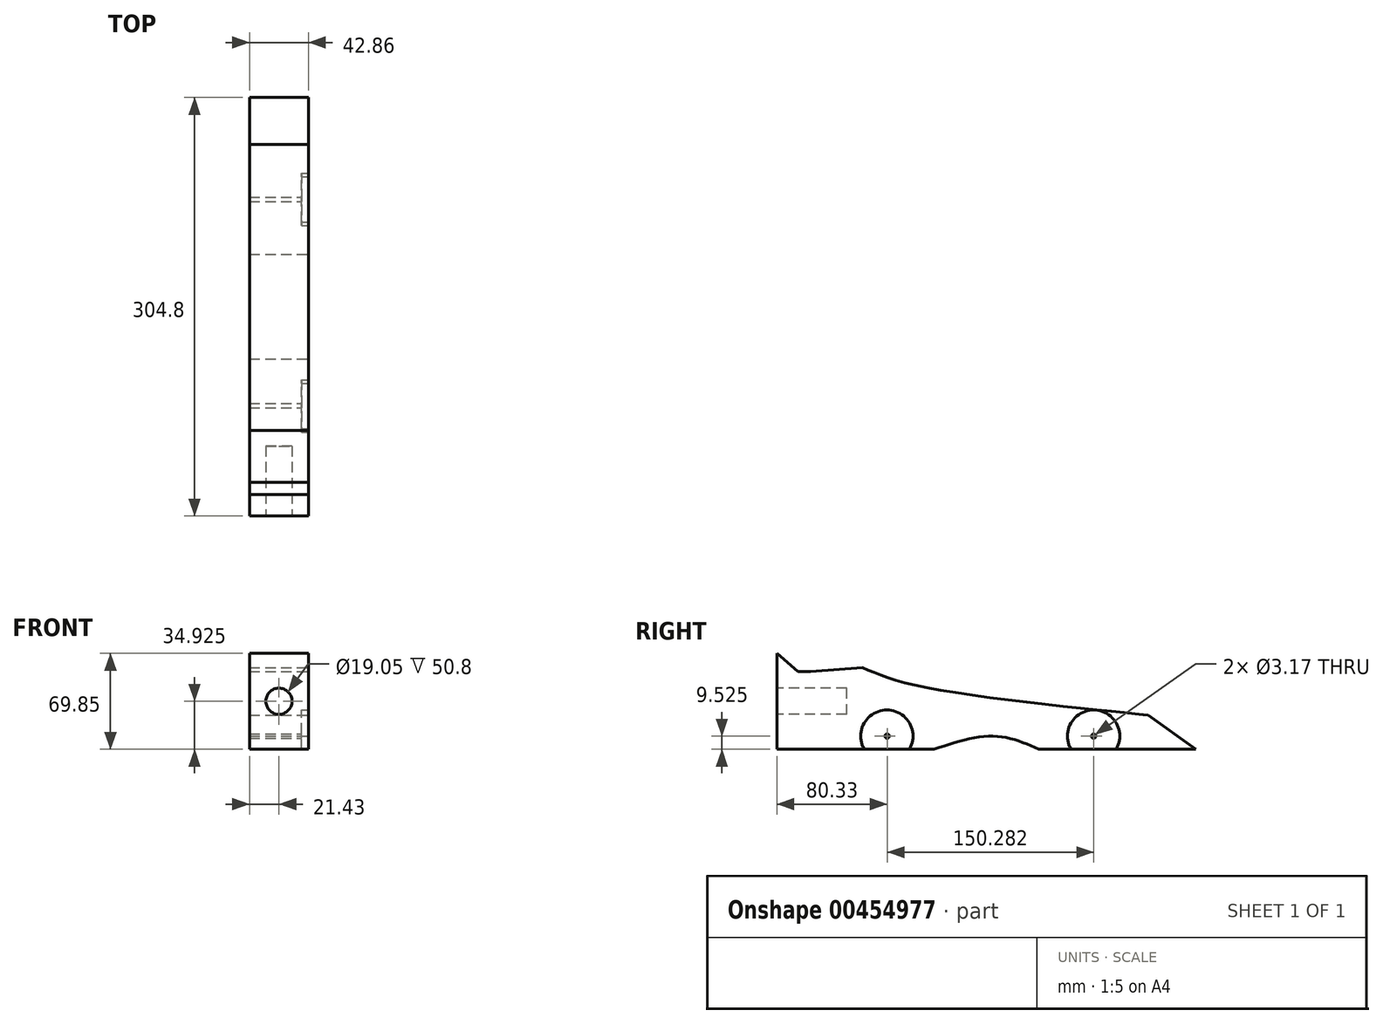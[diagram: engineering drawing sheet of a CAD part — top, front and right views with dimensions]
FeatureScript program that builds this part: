
annotation { "Feature Type Name" : "Feature", "Feature Type Description" : "" }
export const myFeature = defineFeature(function(context is Context, id is Id, definition is map)
    precondition{}
    {
        {
            var Q0;
            Q0=qCreatedBy(makeId("Right.planeOp"),FACE);
            var sketch = newSketch(context, id + "F0", { "sketchPlane" : qUnion([Q0])});
            skLineSegment(sketch, "E0", {"start": v(-152.4, 0) * mm, "end": v(152.4, 0) * mm});
            skLineSegment(sketch, "E1", {"start": v(-152.4, 0) * mm, "end": v(-152.4, 69.85) * mm});
            skLineSegment(sketch, "E2", {"start": v(152.4, 0) * mm, "end": v(152.4, 19.05) * mm});
            skLineSegment(sketch, "E3", {"start": v(152.4, 19.05) * mm, "end": v(-152.4, 69.85) * mm});
            skPoint(sketch, "E4.endSnap0", {"position": v(-152.4, 34.93) * mm});
            skLineSegment(sketch, "E5.0", {"start": v(-95.25, 50.8) * mm, "end": v(-152.4, 50.8) * mm, "construction": true});
            skLineSegment(sketch, "E5.1", {"start": v(-95.25, 50.8) * mm, "end": v(-95.25, 19.05) * mm, "construction": true});
            skLineSegment(sketch, "E5.2", {"start": v(-95.25, 19.05) * mm, "end": v(-152.4, 19.05) * mm, "construction": true});
            skSolve(sketch);
        }
        {
            var Q0;
            Q0=makeQuery(id+"F0.imprint","IMPRINT",FACE,{"disambiguationData":[TD([[makeQuery(id+"F0.imprint","IMPRINT",EDGE,{"derivedFrom":sQuery(id+"F0.wireOp",EDGE,"E0")}),1.0]])]});
            extrude(context, id + "F1", {"entities" : qUnion([Q0]), "depth" : 42.86 * mm, "symmetric" : true});
        }
        {
            var Q0;
            Q0=makeQuery(id+"F1.opExtrude","SWEPT_FACE",FACE,{"disambiguationData":[OSD([sQuery(id+"F0.wireOp",EDGE,"E1")])]});
            var sketch = newSketch(context, id + "F2", { "sketchPlane" : qUnion([Q0])});
            skLineSegment(sketch, "E6", {"start": v(21.43, 34.93) * mm, "end": v(0, 34.93) * mm, "construction": true});
            skCircle(sketch, "E7", {"center": v(0, 34.93) * mm, "radius": 9.53 * mm});
            skSolve(sketch);
        }
        {
            var Q0;
            Q0=makeQuery(id+"F2.imprint","IMPRINT",FACE,{"disambiguationData":[TD([[makeQuery(id+"F2.imprint","IMPRINT",EDGE,{"derivedFrom":sQuery(id+"F2.wireOp",EDGE,"E7")}),1.0]])]});
            var Q1;
            Q1=sQuery(id+"F2.wireOp",EDGE,"E7");
            extrude(context, id + "F3", {"entities" : qUnion([Q0]), "operationType" : NewBodyOperationType.REMOVE, "surfaceEntities" : qUnion([Q1]), "oppositeDirection" : true, "depth" : 50.8 * mm});
        }
        {
            var Q0;
            Q0=makeQuery(id+"F1.opExtrude","CAP_FACE",FACE,{"disambiguationData":[OSD([sQuery(id+"F0.wireOp",EDGE,"E0"),sQuery(id+"F0.wireOp",EDGE,"E1"),sQuery(id+"F0.wireOp",EDGE,"E2"),sQuery(id+"F0.wireOp",EDGE,"E3")])],"isStart":false});
            var sketch = newSketch(context, id + "F4", { "sketchPlane" : qUnion([Q0])});
            skLineSegment(sketch, "E8", {"start": v(-152.4, 34.93) * mm, "end": v(-152.4, 44.45) * mm, "construction": true});
            skLineSegment(sketch, "E9.0", {"start": v(-95.25, 19.05) * mm, "end": v(-152.4, 19.05) * mm, "construction": true});
            skLineSegment(sketch, "E9.1", {"start": v(-95.25, 50.8) * mm, "end": v(-95.25, 19.05) * mm, "construction": true});
            skLineSegment(sketch, "E9.2", {"start": v(-152.4, 50.8) * mm, "end": v(-95.25, 50.8) * mm, "construction": true});
            skLineSegment(sketch, "E10", {"start": v(57.15, 0) * mm, "end": v(57.15, 34.93) * mm, "construction": true});
            skLineSegment(sketch, "E11", {"start": v(-152.4, 44.45) * mm, "end": v(-101.6, 44.45) * mm, "construction": true});
            skLineSegment(sketch, "E12", {"start": v(-101.6, 44.45) * mm, "end": v(-101.6, 25.4) * mm, "construction": true});
            skLineSegment(sketch, "E13", {"start": v(-101.6, 25.4) * mm, "end": v(-152.4, 25.4) * mm, "construction": true});
            skLineSegment(sketch, "E14", {"start": v(118.06, 24.77) * mm, "end": v(152.4, 0) * mm});
            skLineSegment(sketch, "E15", {"start": v(-136.93, 67.27) * mm, "end": v(-136.93, 56.65) * mm});
            skLineSegment(sketch, "E16", {"start": v(-136.93, 56.65) * mm, "end": v(-127.78, 56.65) * mm});
            skLineSegment(sketch, "E17", {"start": v(-127.78, 56.65) * mm, "end": v(-127.78, 65.75) * mm});
            skLineSegment(sketch, "E18", {"start": v(-152.4, 69.85) * mm, "end": v(-136.93, 56.65) * mm});
            skLineSegment(sketch, "E19", {"start": v(-127.78, 56.65) * mm, "end": v(-89.95, 59.44) * mm});
            skFitSpline(sketch, "E20", {"points": [v(-89.95, 59.44) * mm, v(-38.9, 43.98) * mm, v(118.06, 24.77) * mm, v(120.44, 24.38) * mm], "startDerivative": vector(102.3, -45.48) * mm, "endDerivative": vector(15.44, -3.98) * mm});
            skCircle(sketch, "E21", {"center": v(78.21, 9.53) * mm, "radius": 1.59 * mm});
            skLineSegment(sketch, "E22.0.0", {"start": v(152.4, 0) * mm, "end": v(152.4, 19.05) * mm});
            skLineSegment(sketch, "E22.0.1", {"start": v(152.4, 19.05) * mm, "end": v(-152.4, 69.85) * mm});
            skLineSegment(sketch, "E22.0.2", {"start": v(-152.4, 69.85) * mm, "end": v(-152.4, 0) * mm});
            skLineSegment(sketch, "E22.0.3", {"start": v(-152.4, 0) * mm, "end": v(152.4, 0) * mm});
            skLineSegment(sketch, "E23", {"start": v(78.21, 9.53) * mm, "end": v(-85.52, 9.53) * mm, "construction": true});
            skCircle(sketch, "E24", {"center": v(-72.07, 9.53) * mm, "radius": 1.59 * mm});
            skFitSpline(sketch, "E25", {"points": [v(-38, 0) * mm, v(6.04, 9.52) * mm, v(38.28, 0) * mm], "startDerivative": vector(85.43, 28.03) * mm, "endDerivative": vector(66.65, -29.43) * mm});
            skSolve(sketch);
        }
        {
            var Q0;
            Q0=makeQuery(id+"F1.opExtrude","SWEPT_FACE",FACE,{"disambiguationData":[OSD([sQuery(id+"F0.wireOp",EDGE,"E0")])]});
            var sketch = newSketch(context, id + "F5", { "sketchPlane" : qUnion([Q0])});
            skLineSegment(sketch, "E26", {"start": v(0, 152.4) * mm, "end": v(0, -152.4) * mm, "construction": true});
            skLineSegment(sketch, "E27", {"start": v(21.43, -57.15) * mm, "end": v(-21.43, -57.15) * mm, "construction": true});
            skLineSegment(sketch, "E28", {"start": v(15.88, 152.4) * mm, "end": v(15.88, 95.25) * mm, "construction": true});
            skLineSegment(sketch, "E29", {"start": v(15.88, 95.25) * mm, "end": v(-15.87, 95.25) * mm, "construction": true});
            skLineSegment(sketch, "E30", {"start": v(-15.87, 95.25) * mm, "end": v(-15.87, 152.4) * mm, "construction": true});
            skLineSegment(sketch, "E31", {"start": v(0, 152.4) * mm, "end": v(-9.53, 152.4) * mm, "construction": true});
            skLineSegment(sketch, "E32", {"start": v(-9.53, 152.4) * mm, "end": v(-9.53, 101.6) * mm, "construction": true});
            skLineSegment(sketch, "E33", {"start": v(-9.52, 101.6) * mm, "end": v(9.53, 101.6) * mm, "construction": true});
            skLineSegment(sketch, "E34", {"start": v(9.53, 101.6) * mm, "end": v(9.53, 152.4) * mm, "construction": true});
            skSolve(sketch);
        }
        {
            var Q0;
            Q0=makeQuery(id+"F4.imprint","IMPRINT",FACE,{"disambiguationData":[TD([[makeQuery(id+"F4.imprint","IMPRINT",EDGE,{"derivedFrom":sQuery(id+"F4.wireOp",EDGE,"E14")}),-1.0]])]});
            extrude(context, id + "F6", {"entities" : qUnion([Q0]), "operationType" : NewBodyOperationType.INTERSECT, "oppositeDirection" : true, "depth" : 43.18 * mm});
        }
        {
            var Q0;
            Q0=makeQuery(id+"F4.imprint","IMPRINT",FACE,{"disambiguationData":[TD([[makeQuery(id+"F4.imprint","IMPRINT",EDGE,{"derivedFrom":sQuery(id+"F4.wireOp",EDGE,"E14")}),-1.0]])]});
            var sketch = newSketch(context, id + "F7", { "sketchPlane" : qUnion([Q0])});
            skCircle(sketch, "E35", {"center": v(-72.29, 9.52) * mm, "radius": 19.05 * mm});
            skCircle(sketch, "E36", {"center": v(78.21, 9.52) * mm, "radius": 19.05 * mm});
            skSolve(sketch);
        }
        {
            var Q0;
            Q0 = qSketchRegion(id + "F7", true);
            extrude(context, id + "F8", {"entities" : qUnion([Q0]), "operationType" : NewBodyOperationType.REMOVE, "oppositeDirection" : true, "depth" : 5.08 * mm});
        }
    });
